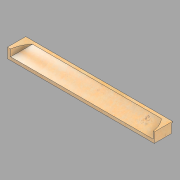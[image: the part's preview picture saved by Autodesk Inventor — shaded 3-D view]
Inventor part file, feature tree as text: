
AUTODESK INVENTOR PART (.ipt)
format: ipt  version: 2022.2 (Build 262287010, 287A)  size: 134,144 bytes
history: native  units: in
note: dims shown in document units (in); Inventor stores cm internally (conversion verified against a paired STEP export)
features: revolve x2, other x1, direct_edit x1
ambient origin geometry x8: Origin, YZ Plane, XZ Plane, XY Plane, X Axis, Y Axis, Z Axis, Center Point
bodies: Solid1 (feature_tree)
feature tree (4):
  other  "Head (R)"
  direct_edit  "Direct Edit1"
  revolve  "Rotate1"  Angle=180.0deg
  revolve  "Rotate2"  [1 undecoded]
note: 1 required parameter value undecoded (feature->parameter linkage not recoverable at this tier; creation-order binding heuristic only, values carry confidence <= 0.55)
